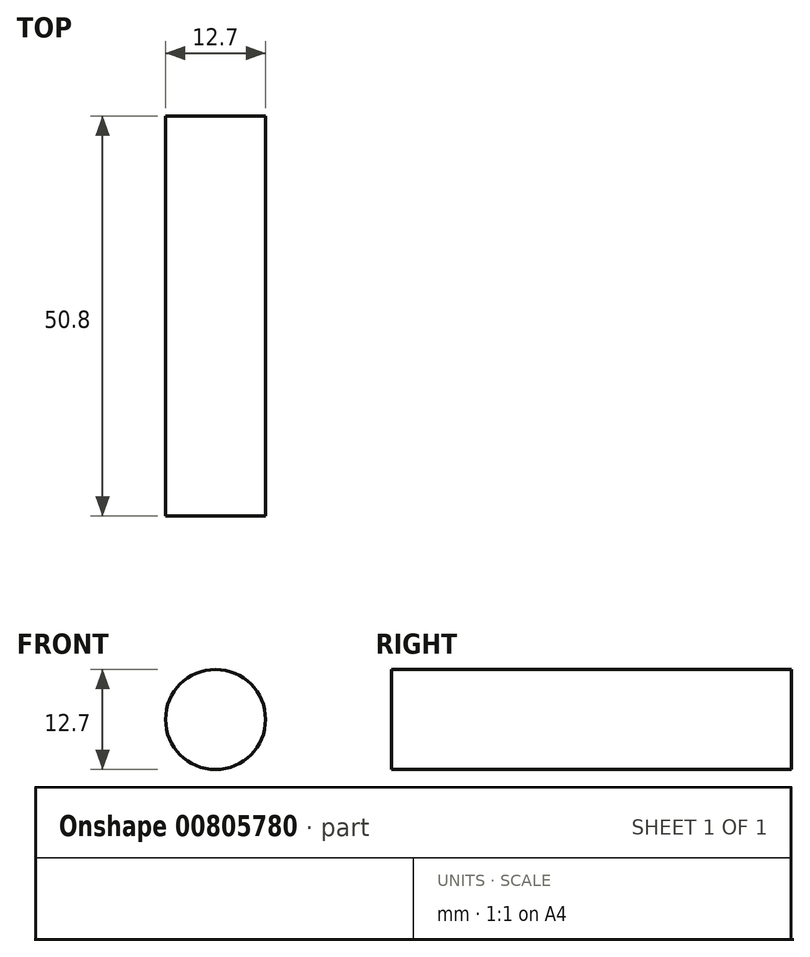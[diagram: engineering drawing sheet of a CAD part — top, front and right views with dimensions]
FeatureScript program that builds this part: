
annotation { "Feature Type Name" : "Feature", "Feature Type Description" : "" }
export const myFeature = defineFeature(function(context is Context, id is Id, definition is map)
    precondition{}
    {
        {
            var Q0;
            Q0=qCreatedBy(makeId("Front.planeOp"),FACE);
            var sketch = newSketch(context, id + "F0", { "sketchPlane" : qUnion([Q0])});
            skCircle(sketch, "E0", {"center": v(0, 0) * mm, "radius": 6.35 * mm});
            skSolve(sketch);
        }
        {
            var Q0;
            Q0=makeQuery(id+"F0.imprint","IMPRINT",FACE,{"disambiguationData":[TD([[makeQuery(id+"F0.imprint","IMPRINT",EDGE,{"derivedFrom":sQuery(id+"F0.wireOp",EDGE,"E0")}),1.0]])]});
            extrude(context, id + "F1", {"entities" : qUnion([Q0]), "depth" : 50.8 * mm, "offsetDistance" : 25.4 * mm});
        }
    });
